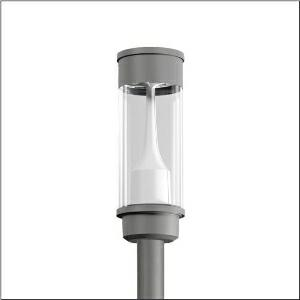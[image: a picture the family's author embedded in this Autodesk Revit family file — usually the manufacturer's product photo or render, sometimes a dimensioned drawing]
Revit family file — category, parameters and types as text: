
# Revit family: litepole_iq___st1_2a_5xa5415ef14hp_af4c
name_source: partatom
category: Lighting Fixtures
units: mm (PartAtom-declared; Revit-internal decimal feet)

## family parameters
Cut with Voids When Loaded = No
Host = Face
Light Source = No
Part Type = Normal
Room Calculation Point = No
Round Connector Dimension = Use Diameter
Shared = No

## types (1)
- --- (1 x LED, 4730 lm, 33.6 W, 3000K)
    Apparent Load = 34 VA
    CIE Flux Codes = 22 60 93 95 100
    Color Rendering = 70
    Color Temperature = 3000K
    Default Elevation = 1800 mm
    Description = Litepole iQ, mast luminaire, Module 540 iQ-SR, primary light control with 3 zone facetted reflector, of plastic, silver coated, highly specular, structured, primary optical cover: cover, of PMMA, transparent, partly coated, light distribution: ST1.2a, light emission: direct distribution, primary light characteristic: asymmetric, installation type: post-top, LED, High Power LED, rated luminous flux: 4.730lm, luminous efficacy: 141lm/W, light colour: 730, colour temperature: 3000K, control gear: iQ Street-Remote, control: optimised constant luminous flux control (CLO 2.0), Desk-Remote (wireless, voltage-free reading and setting of iQ features in the workshop via application-optimized NFC function/RFID function), Light-Fading, Smart-Wire, Night-Set, Lumen-Switch, Temp-Guard, Auto-Match, Street-Remote, pre-setting: logarithmic dimming characteristic, with terminal, 6-pole, max. 2.5mm², mains connection: 230..240V, AC, 50/60Hz, start of lifetime: 34W, end of service life: 36W, reduction: 15W, luminaire housing, upper part, of glass-fibre reinforced polyester, coated, Siteco® metallic grey (DB 702S), diameter: 210mm, height: 590mm, spigot size: d x l = 76 x 70mm (post-top) | with reducer (optional accessory) 60 x 70mm, mounting height: 3..5m, post-top mast mounting element, of diecast aluminium, coated, Siteco® metallic grey (DB 702S), Module 540 iQ-SR, traffic white (RAL 9016), equipment: Power, protection rating (complete): IP65, insulation class (complete): insulation class II (safety insulation), certification: CE, ENEC, VDE, packaging unit: 1 piece

Light Distribution: ST1.2a
    Height = 590 mm
    Lamp = 1 x LED
    Lamp Light Flux = 4730 lm
    Lamp Power = 33.6 W
    Lamp count = 1
    Length = 220 mm
    Luminous efficacy = 141 lm/W
    Manufacturer = Siteco
    ModVariant = No
    Model = 5XA5415EF14HP
    Number of Poles = 1
    OnlyDefault = Yes
    Power Factor = 1
    Product Name = Litepole iQ | ST1.2a
    Product group = mast luminaire | pylon top
    ProductGroupID = 6100
    Protection Class = Protection class II
    Protection Degree = IP 65
    RLX_Detail_Level = 1
    RLX_Emergency_Light_Flux = 0 lm
    RLX_Emergency_Type = 0
    RLX_Emergency_Type_DB = No
    RlxData = <blob elided: 29765 chars, md5=b0c8b2ac>
    Socket = socket
    Standby Power = 0 W
    System Light Flux = 4730 lm
    System Power = 34 W
    Type Comments = factory setting: luminous flux: 100 % | dim-lin: 254 | 695 mA
    Type Image = l_1006025.jpg
    URL = http://relux.com
    VarID = @adj_216349
    Voltage = 0 V
    Weight = 0.00 kg
    Width = 0 mm  [stored 0 ft]

note: [stored X ft] marks values corroborated as IEEE doubles in the binary element streams (Revit-internal decimal feet)

## geometry (parser evidence)
native form markers: Blend x4, Sweep x8
no freeform markers — native parametric forms only
